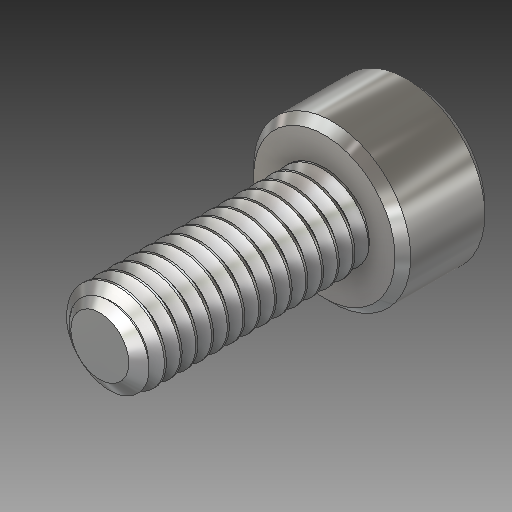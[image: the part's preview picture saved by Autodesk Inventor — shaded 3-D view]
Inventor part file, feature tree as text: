
AUTODESK INVENTOR PART (.ipt)
format: ipt  version: 2019.4 (Build 234330000, 330)  size: 621,056 bytes
history: native  units: in
note: dims shown in document units (in); Inventor stores cm internally (conversion verified against a paired STEP export)
features: chamfer x1
ambient origin geometry x8: Origin, YZ Plane, XZ Plane, XY Plane, X Axis, Y Axis, Z Axis, Center Point
bodies: Solid1 (feature_tree)
feature tree (1):
  chamfer  "Chamfer1"  [1 undecoded]
note: 1 required parameter value undecoded (feature->parameter linkage not recoverable at this tier; creation-order binding heuristic only, values carry confidence <= 0.55)
